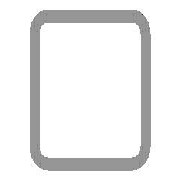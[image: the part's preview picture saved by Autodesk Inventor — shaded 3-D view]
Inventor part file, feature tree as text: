
AUTODESK INVENTOR PART (.ipt)
format: ipt  version: 2025 (Build 290162010, 162A)  size: 133,632 bytes
history: native  units: mm (DEFAULTED — no unit token found)
features: other x4, sketch x1, plane x1
ambient origin geometry x8: Origin, YZ Plane, XZ Plane, XY Plane, X Axis, Y Axis, Z Axis, Center Point
bodies: Solid1 (feature_tree), Body (feature_tree)
feature tree (6):
  parser-record x1  (decoder bookkeeping rows leaked as tree rows — omitted from the tree; the rows remain in map.json)
  other  "Driven Length"
  other  "Start Plane"
  other  "End Plane"
  sketch  "Sketch3"  dims[d3=565.0mm d4=0.0mm d7=4.0mm d9=40.0mm d11=40.0mm d12=2.0mm d13=40.0mm d14=605.0mm d15=20.0mm d16=20.0mm d17=90.0deg d18=565.0mm]
  plane  "Work Plane3"
